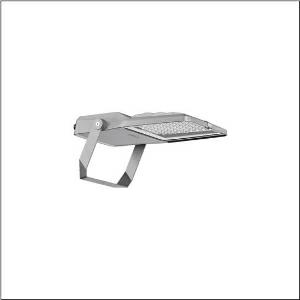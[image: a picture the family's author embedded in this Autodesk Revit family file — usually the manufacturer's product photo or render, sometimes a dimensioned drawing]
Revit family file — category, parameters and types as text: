
# Revit family: floodlight_fl_21_iq_mini___pl64_5xa7772b4e1a_46a5
name_source: partatom
category: Lighting Fixtures
units: mm (PartAtom-declared; Revit-internal decimal feet)

## family parameters
Cut with Voids When Loaded = No
Host = Face
Light Source = No
Part Type = Normal
Room Calculation Point = No
Round Connector Dimension = Use Diameter
Shared = No

## types (1)
- --- (1 x LED, 6270 lm, 45.5 W, 4000K)
    Apparent Load = 46 VA
    CIE Flux Codes = 28 80 98 100 100
    Color Rendering = 70
    Color Temperature = 4000K
    Default Elevation = 1800 mm
    Description = Floodlight FL 21 iQ mini, floodlight, primary light control with lens, of PMMA, primary optical cover: protective disc, of toughened safety glass, transparent, light distribution: PL64, light emission: direct distribution, installation type: surface-mounted, LED, High Power LED, rated luminous flux: 6.270lm, luminous efficacy: 138lm/W, light colour: 740, colour temperature: 4000K, control gear: iQ Street-Remote/DALI, control: Street-Remote, Auto-Match, Temp-Guard, Night-Set, Smart-Wire, Desk-Remote (wireless, voltage-free reading and setting of iQ features in the workshop via application-optimized NFC function/RFID function), optimised constant luminous flux control (CLO 2.0), with terminal, 6-pole, mains connection: 220..240V, AC, 50/60Hz, start of lifetime: 46W, end of service life: 48W, reduction: 22W, luminaire housing, of diecast aluminium, powder-coated, Siteco® metallic grey (DB 702S), corrosivity category C5 mid according to DIN EN ISO 12944, suitable for swimming pools, chlorine-resistant, sealing non-destructively replaceable, mounting bracket, of steel, galvanised, powder-coated, Siteco® metallic grey (DB 702S), protection rating (complete): IP66, insulation class (complete): insulation class II (safety insulation), certification: CE, ENEC, VDE, protection symbol: D, impact resistance: IK08, permissible operating ambient temperature: -40..+40°C, permissible operating ambient temperature for outdoor applications: -40..+50°C, standard: DIN EN 12944, LABS conformity tested according to VDMA 24364:2018-05, packaging unit: 1 piece

Light Distribution: PL64
    Height = 70 mm
    Lamp = 1 x LED
    Lamp Light Flux = 6270 lm
    Lamp Power = 45.5 W
    Lamp count = 1
    Length = 485 mm
    Luminous efficacy = 138 lm/W
    Manufacturer = Siteco
    ModVariant = No
    Model = 5XA7772B4E1A
    Number of Poles = 1
    OnlyDefault = Yes
    Power Factor = 1
    Product Name = Floodlight FL 21 iQ mini | PL64
    Product group = floodlight | pylon annexe
    ProductGroupID = 6200
    Protection Class = Protection class II
    Protection Degree = IP 66
    RLX_Detail_Level = 1
    RLX_Emergency_Light_Flux = 0 lm
    RLX_Emergency_Type = 0
    RLX_Emergency_Type_DB = No
    RlxData = <blob elided: 96197 chars, md5=b65a144b>
    Socket = socket
    Standby Power = 0 W
    System Light Flux = 6270 lm
    System Power = 46 W
    Type Comments = factory setting: luminous flux: 100 % | dim-lin: 254 | 463 mA
    Type Image = l_1006845.jpg
    URL = http://relux.com
    VarID = @adj_166830
    Voltage = 0 V
    Weight = 0.00 kg
    Width = 337 mm

## geometry (parser evidence)
native form markers: Blend x4, Sweep x12
no freeform markers — native parametric forms only
